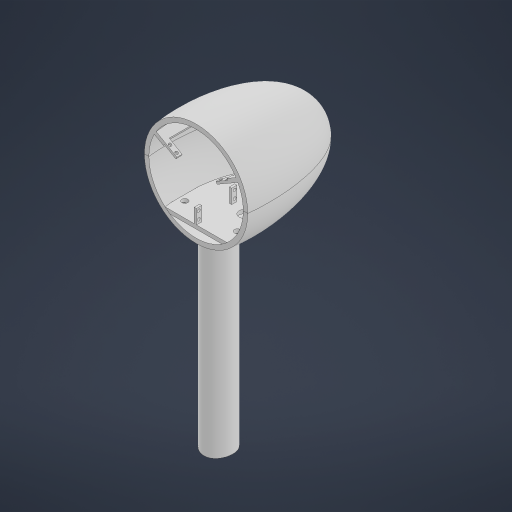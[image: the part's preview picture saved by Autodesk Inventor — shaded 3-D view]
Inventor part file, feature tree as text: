
AUTODESK INVENTOR PART (.ipt)
format: ipt  version: 2023.2 (Build 272271000, 271)  size: 754,176 bytes
history: native  units: mm
features: extrude x10, sketch x7, other x6, revolve x2, shell x2, mirror x2, pattern_circular x1
ambient origin geometry x8: Origin, YZ Plane, XZ Plane, XY Plane, X Axis, Y Axis, Z Axis, Center Point
bodies: Body1 (feature_tree), Body2 (feature_tree), Body3 (feature_tree), Body4 (feature_tree)
feature tree (30):
  other  "Gehäuse unten"
  sketch  "Skizze1"  dims[d3=160.0mm d29=180.0deg d30=6.0mm]
  revolve  "Umdrehung3"
  shell  "Wandung4"  Thickness=80.0mm
  extrude  "Extrusion4"  TaperAngle=180.0deg  [1 undecoded]
  mirror  "Spiegeln1"
  revolve  "Umdrehung4"
  shell  "Wandung5"  Thickness=6.0mm
  extrude  "Extrusion5"  Depth=3.1mm
  mirror  "Spiegeln2"
  other  "Körper verschieben3"
  extrude  "Extrusion6"  Depth=3.1mm
  extrude  "Extrusion7"  Depth=3.1mm
  extrude  "Extrusion8"  Depth=10.0mm
  extrude  "Extrusion9"  Depth=10.0mm
  extrude  "Extrusion11"  Depth=30.0mm
  other  "Arbeitsachse1"
  pattern_circular  "Runde Anordnung1"  [2 undecoded]
  extrude  "Extrusion12"  Depth=30.0mm
  extrude  "Extrusion13"  Depth=30.0mm
  extrude  "Extrusion14"  Depth=30.0mm
  other  "Gehäuse oben"
  sketch  "Skizze17"  dims[d31=3.0mm d32=3.1mm]
  other  "Turm"
  sketch  "Skizze18"  dims[d33=5.0mm d34=3.1mm]
  sketch  "Skizze26"  dims[d35=3.1mm d37=3.1mm]
  sketch  "Skizze27"  dims[d38=10.0mm d39=10.0mm]
  sketch  "Skizze28"  dims[d40=10.0mm d41=3.1mm]
  sketch  "Skizze29"  dims[d42=3.1mm d43=3.1mm d44=3.1mm d45=3.1mm d46=3.1mm d47=3.1mm d48=3.1mm d49=3.1mm d50=3.1mm d51=10.0mm d52=10.0mm d53=10.0mm d54=10.0mm d55=10.0mm d56=10.0mm d57=10.0mm d58=10.0mm d59=10.0mm d61=3.1mm d62=3.1mm d63=10.0mm d64=10.0mm d65=10.0mm d66=3.1mm d67=3.1mm d68=0.0mm d69=180.0deg d70=6.0mm d71=3.1mm d72=0.0mm d73=0.0mm d74=0.0001mm d75=0.0mm d82=5.0mm d83=50.0mm d84=85.0mm d85=10.0mm d86=0.0mm d87=39.0mm d88=250.0mm d89=0.0mm d90=5.7mm d91=0.0mm d92=0.0mm d93=30.0deg d94=120.0deg d96=55.0mm d97=2.5mm d98=31.0mm d100=18.0mm d102=2.0mm d103=20.0mm d105=120.0deg d107=54.0mm d108=0.0mm d113=20.0mm d114=40.0mm d115=7.0mm d116=7.0mm d117=0.0mm d118=20.0mm d119=120.0deg d121=4.0mm d122=4.0mm d123=4.0mm d124=20.0mm d126=48.0mm d127=20.0mm d129=10.0mm d132=50.0mm d133=0.5mm d134=2.5mm d136=54.0mm d137=0.0mm d138=40.0mm d139=19.0mm d140=7.0mm d141=4.0mm d142=4.0mm d143=4.0mm d144=20.0mm d146=48.0mm d147=20.0mm d149=10.0mm d152=10.0mm d153=0.0mm d154=8.0mm d155=20.0mm d156=35.0mm d157=7.0mm d158=0.0mm d159=8.0mm d160=13.0mm d161=62.2mm d162=15.0mm d163=45.0mm d164=20.0mm d165=19.0mm d166=30.0mm d167=90.0deg d168=23.911011mm d169=23.212879mm d170=40.5mm d172=69.0mm d175=90.0deg d177=140.0mm d178=38.0mm d179=90.0deg d180=77.358929mm d181=25.00527mm]
  other  "Platte"
note: 3 required parameter values undecoded (feature->parameter linkage not recoverable at this tier; creation-order binding heuristic only, values carry confidence <= 0.55)
